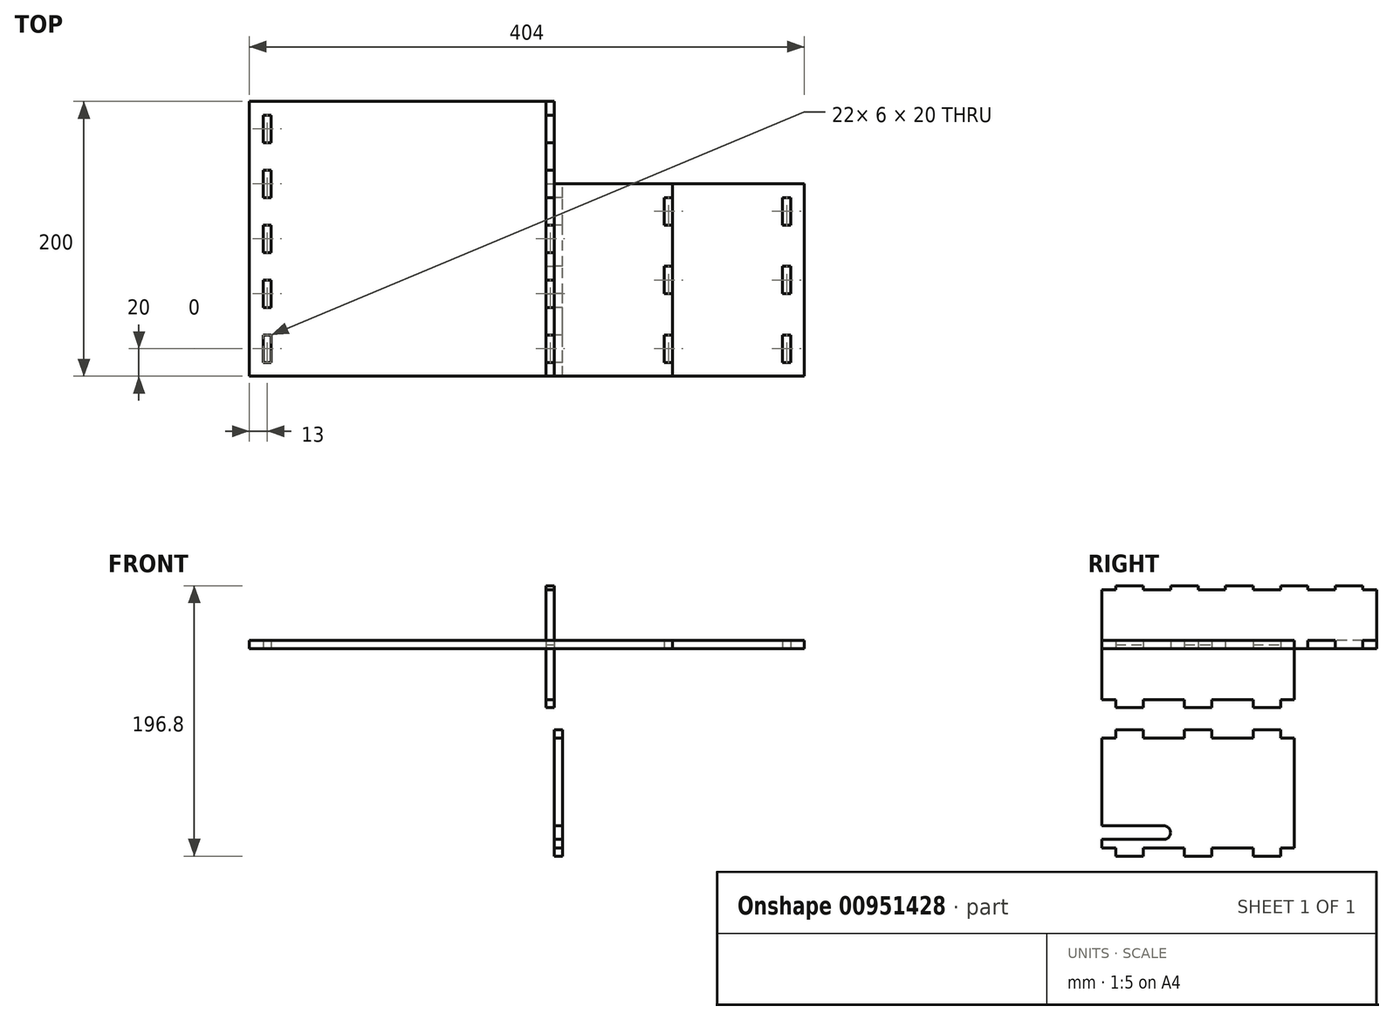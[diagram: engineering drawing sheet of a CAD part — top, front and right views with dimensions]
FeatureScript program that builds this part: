
annotation { "Feature Type Name" : "Feature", "Feature Type Description" : "" }
export const myFeature = defineFeature(function(context is Context, id is Id, definition is map)
    precondition{}
    {
        {
            var Q0;
            Q0=qCreatedBy(makeId("Top.planeOp"),FACE);
            var sketch = newSketch(context, id + "F0", { "sketchPlane" : qUnion([Q0])});
            skLineSegment(sketch, "E0.bottom", {"start": v(0, 200) * mm, "end": v(-222, 200) * mm});
            skLineSegment(sketch, "E0.top", {"start": v(-222, 0) * mm, "end": v(0, 0) * mm});
            skLineSegment(sketch, "E0.left", {"start": v(-222, 200) * mm, "end": v(-222, 0) * mm});
            skLineSegment(sketch, "E0.right", {"start": v(0, 200) * mm, "end": v(0, 0) * mm});
            skLineSegment(sketch, "E1.bottom", {"start": v(0, 0) * mm, "end": v(172, 0) * mm});
            skLineSegment(sketch, "E1.top", {"start": v(0, 140) * mm, "end": v(172, 140) * mm});
            skLineSegment(sketch, "E1.left", {"start": v(0, 0) * mm, "end": v(0, 140) * mm});
            skLineSegment(sketch, "E1.right", {"start": v(172, 0) * mm, "end": v(172, 140) * mm});
            skLineSegment(sketch, "E2.bottom", {"start": v(0, 0) * mm, "end": v(86, 0) * mm});
            skLineSegment(sketch, "E2.top", {"start": v(0, 140) * mm, "end": v(86, 140) * mm});
            skLineSegment(sketch, "E2.right", {"start": v(86, 0) * mm, "end": v(86, 140) * mm});
            skPoint(sketch, "E3.end.orphan", {"position": v(-212, 0) * mm});
            skLineSegment(sketch, "E4.bottom", {"start": v(-212, 190) * mm, "end": v(-206, 190) * mm});
            skLineSegment(sketch, "E4.top", {"start": v(-212, 170) * mm, "end": v(-206, 170) * mm});
            skLineSegment(sketch, "E4.left", {"start": v(-212, 190) * mm, "end": v(-212, 170) * mm});
            skLineSegment(sketch, "E4.right", {"start": v(-206, 190) * mm, "end": v(-206, 170) * mm});
            skLineSegment(sketch, "E5.0.1.0", {"start": v(-212, 150) * mm, "end": v(-212, 130) * mm});
            skLineSegment(sketch, "E5.0.1.1", {"start": v(-206, 150) * mm, "end": v(-206, 130) * mm});
            skLineSegment(sketch, "E5.0.1.2", {"start": v(-212, 150) * mm, "end": v(-206, 150) * mm});
            skLineSegment(sketch, "E5.0.1.3", {"start": v(-212, 130) * mm, "end": v(-206, 130) * mm});
            skLineSegment(sketch, "E5.0.2.0", {"start": v(-212, 110) * mm, "end": v(-212, 90) * mm});
            skLineSegment(sketch, "E5.0.2.1", {"start": v(-206, 110) * mm, "end": v(-206, 90) * mm});
            skLineSegment(sketch, "E5.0.2.2", {"start": v(-212, 110) * mm, "end": v(-206, 110) * mm});
            skLineSegment(sketch, "E5.0.2.3", {"start": v(-212, 90) * mm, "end": v(-206, 90) * mm});
            skLineSegment(sketch, "E5.0.3.0", {"start": v(-212, 70) * mm, "end": v(-212, 50) * mm});
            skLineSegment(sketch, "E5.0.3.1", {"start": v(-206, 70) * mm, "end": v(-206, 50) * mm});
            skLineSegment(sketch, "E5.0.3.2", {"start": v(-212, 70) * mm, "end": v(-206, 70) * mm});
            skLineSegment(sketch, "E5.0.3.3", {"start": v(-212, 50) * mm, "end": v(-206, 50) * mm});
            skLineSegment(sketch, "E5.0.4.0", {"start": v(-212, 30) * mm, "end": v(-212, 10) * mm});
            skLineSegment(sketch, "E5.0.4.1", {"start": v(-206, 30) * mm, "end": v(-206, 10) * mm});
            skLineSegment(sketch, "E5.0.4.2", {"start": v(-212, 30) * mm, "end": v(-206, 30) * mm});
            skLineSegment(sketch, "E5.0.4.3", {"start": v(-212, 10) * mm, "end": v(-206, 10) * mm});
            skLineSegment(sketch, "E5.direction1", {"start": v(-212, 170) * mm, "end": v(-187, 170) * mm, "construction": true});
            skLineSegment(sketch, "E5.direction2", {"start": v(-212, 170) * mm, "end": v(-212, 130) * mm, "construction": true});
            skPoint(sketch, "E6.start.orphan", {"position": v(-6, 200) * mm});
            skLineSegment(sketch, "E7.bottom", {"start": v(0, 190) * mm, "end": v(-6, 190) * mm});
            skLineSegment(sketch, "E7.top", {"start": v(0, 170) * mm, "end": v(-6, 170) * mm});
            skLineSegment(sketch, "E7.left", {"start": v(0, 190) * mm, "end": v(0, 170) * mm});
            skLineSegment(sketch, "E7.right", {"start": v(-6, 190) * mm, "end": v(-6, 170) * mm});
            skLineSegment(sketch, "E8.0.1.0", {"start": v(0, 150) * mm, "end": v(0, 130) * mm});
            skLineSegment(sketch, "E8.0.1.1", {"start": v(0, 130) * mm, "end": v(-6, 130) * mm});
            skLineSegment(sketch, "E8.0.1.2", {"start": v(-6, 150) * mm, "end": v(-6, 130) * mm});
            skLineSegment(sketch, "E8.0.1.3", {"start": v(0, 150) * mm, "end": v(-6, 150) * mm});
            skLineSegment(sketch, "E8.0.2.0", {"start": v(0, 110) * mm, "end": v(0, 90) * mm});
            skLineSegment(sketch, "E8.0.2.1", {"start": v(0, 90) * mm, "end": v(-6, 90) * mm});
            skLineSegment(sketch, "E8.0.2.2", {"start": v(-6, 110) * mm, "end": v(-6, 90) * mm});
            skLineSegment(sketch, "E8.0.2.3", {"start": v(0, 110) * mm, "end": v(-6, 110) * mm});
            skLineSegment(sketch, "E8.0.3.0", {"start": v(0, 70) * mm, "end": v(0, 50) * mm});
            skLineSegment(sketch, "E8.0.3.1", {"start": v(0, 50) * mm, "end": v(-6, 50) * mm});
            skLineSegment(sketch, "E8.0.3.2", {"start": v(-6, 70) * mm, "end": v(-6, 50) * mm});
            skLineSegment(sketch, "E8.0.3.3", {"start": v(0, 70) * mm, "end": v(-6, 70) * mm});
            skLineSegment(sketch, "E8.0.4.0", {"start": v(0, 30) * mm, "end": v(0, 10) * mm});
            skLineSegment(sketch, "E8.0.4.1", {"start": v(0, 10) * mm, "end": v(-6, 10) * mm});
            skLineSegment(sketch, "E8.0.4.2", {"start": v(-6, 30) * mm, "end": v(-6, 10) * mm});
            skLineSegment(sketch, "E8.0.4.3", {"start": v(0, 30) * mm, "end": v(-6, 30) * mm});
            skLineSegment(sketch, "E8.direction1", {"start": v(-6, 170) * mm, "end": v(19, 170) * mm, "construction": true});
            skLineSegment(sketch, "E8.direction2", {"start": v(-6, 170) * mm, "end": v(-6, 130) * mm, "construction": true});
            skLineSegment(sketch, "E9.bottom", {"start": v(172, 10) * mm, "end": v(166, 10) * mm});
            skLineSegment(sketch, "E9.top", {"start": v(172, 30) * mm, "end": v(166, 30) * mm});
            skLineSegment(sketch, "E9.left", {"start": v(172, 10) * mm, "end": v(172, 30) * mm});
            skLineSegment(sketch, "E9.right", {"start": v(166, 10) * mm, "end": v(166, 30) * mm});
            skLineSegment(sketch, "E10.0.1.0", {"start": v(172, 80) * mm, "end": v(166, 80) * mm});
            skLineSegment(sketch, "E10.0.1.1", {"start": v(172, 60) * mm, "end": v(166, 60) * mm});
            skLineSegment(sketch, "E10.0.1.2", {"start": v(166, 60) * mm, "end": v(166, 80) * mm});
            skLineSegment(sketch, "E10.0.1.3", {"start": v(172, 60) * mm, "end": v(172, 80) * mm});
            skLineSegment(sketch, "E10.0.2.0", {"start": v(172, 130) * mm, "end": v(166, 130) * mm});
            skLineSegment(sketch, "E10.0.2.1", {"start": v(172, 110) * mm, "end": v(166, 110) * mm});
            skLineSegment(sketch, "E10.0.2.2", {"start": v(166, 110) * mm, "end": v(166, 130) * mm});
            skLineSegment(sketch, "E10.0.2.3", {"start": v(172, 110) * mm, "end": v(172, 130) * mm});
            skLineSegment(sketch, "E10.1.0.0", {"start": v(86, 30) * mm, "end": v(80, 30) * mm});
            skLineSegment(sketch, "E10.1.0.1", {"start": v(86, 10) * mm, "end": v(80, 10) * mm});
            skLineSegment(sketch, "E10.1.0.2", {"start": v(80, 10) * mm, "end": v(80, 30) * mm});
            skLineSegment(sketch, "E10.1.0.3", {"start": v(86, 10) * mm, "end": v(86, 30) * mm});
            skLineSegment(sketch, "E10.1.1.0", {"start": v(86, 80) * mm, "end": v(80, 80) * mm});
            skLineSegment(sketch, "E10.1.1.1", {"start": v(86, 60) * mm, "end": v(80, 60) * mm});
            skLineSegment(sketch, "E10.1.1.2", {"start": v(80, 60) * mm, "end": v(80, 80) * mm});
            skLineSegment(sketch, "E10.1.1.3", {"start": v(86, 60) * mm, "end": v(86, 80) * mm});
            skLineSegment(sketch, "E10.1.2.0", {"start": v(86, 130) * mm, "end": v(80, 130) * mm});
            skLineSegment(sketch, "E10.1.2.1", {"start": v(86, 110) * mm, "end": v(80, 110) * mm});
            skLineSegment(sketch, "E10.1.2.2", {"start": v(80, 110) * mm, "end": v(80, 130) * mm});
            skLineSegment(sketch, "E10.1.2.3", {"start": v(86, 110) * mm, "end": v(86, 130) * mm});
            skLineSegment(sketch, "E10.direction1", {"start": v(166, 10) * mm, "end": v(80, 10) * mm, "construction": true});
            skLineSegment(sketch, "E10.direction2", {"start": v(166, 10) * mm, "end": v(166, 60) * mm, "construction": true});
            skLineSegment(sketch, "E11.bottom", {"start": v(172, 140) * mm, "end": v(182, 140) * mm});
            skLineSegment(sketch, "E11.top", {"start": v(172, 0) * mm, "end": v(182, 0) * mm});
            skLineSegment(sketch, "E11.left", {"start": v(172, 140) * mm, "end": v(172, 0) * mm});
            skLineSegment(sketch, "E11.right", {"start": v(182, 140) * mm, "end": v(182, 0) * mm});
            skSolve(sketch);
        }
        {
            var Q0;
            Q0=makeQuery(id+"F0.imprint","IMPRINT",FACE,{"disambiguationData":[TD([[makeQuery(id+"F0.imprint","IMPRINT",EDGE,{"derivedFrom":sQuery(id+"F0.wireOp",EDGE,"E0.bottom")}),-1.0]])]});
            var Q1;
            {var subQ10=sQuery(id+"F0.wireOp",EDGE,"E9.bottom");Q1=makeQuery(id+"F0.imprint","IMPRINT",FACE,{"disambiguationData":[TD([[makeQuery(id+"F0.imprint","IMPRINT",EDGE,{"derivedFrom":subQ10}),1.0]])]});}
            var Q2;
            {var subQ14=sQuery(id+"F0.wireOp",EDGE,"E10.1.0.0");Q2=makeQuery(id+"F0.imprint","IMPRINT",FACE,{"disambiguationData":[TD([[makeQuery(id+"F0.imprint","IMPRINT",EDGE,{"derivedFrom":subQ14}),-1.0]])]});}
            var Q3;
            {var subQ5=sQuery(id+"F0.wireOp",EDGE,"E0.bottom");Q3=makeQuery(id+"F0.imprint","IMPRINT",FACE,{"disambiguationData":[TD([[makeQuery(id+"F0.imprint","IMPRINT",EDGE,{"derivedFrom":subQ5}),1.0]])]});}
            var Q4;
            {var subQ5=sQuery(id+"F0.wireOp",EDGE,"E0.bottom");Q4=makeQuery(id+"F0.imprint","IMPRINT",FACE,{"disambiguationData":[TD([[makeQuery(id+"F0.imprint","IMPRINT",EDGE,{"derivedFrom":subQ5}),1.0]])]});}
            var Q5;
            {var subQ7=sQuery(id+"F0.wireOp",EDGE,"E11.bottom");Q5=makeQuery(id+"F0.imprint","IMPRINT",FACE,{"disambiguationData":[TD([[makeQuery(id+"F0.imprint","IMPRINT",EDGE,{"derivedFrom":subQ7}),-1.0]])]});}
            extrude(context, id + "F1", {"entities" : qUnion([Q0, Q1, Q2, Q3, Q4, Q5]), "depth" : 6 * mm, "offsetDistance" : 25 * mm});
        }
        {
            var Q0;
            Q0=makeQuery(id+"F0.imprint","IMPRINT",FACE,{"disambiguationData":[TD([[makeQuery(id+"F0.imprint","IMPRINT",EDGE,{"derivedFrom":sQuery(id+"F0.wireOp",EDGE,"E0.bottom")}),-1.0]])]});
            var Q1;
            {var subQ14=sQuery(id+"F0.wireOp",EDGE,"E10.1.0.0");Q1=makeQuery(id+"F0.imprint","IMPRINT",FACE,{"disambiguationData":[TD([[makeQuery(id+"F0.imprint","IMPRINT",EDGE,{"derivedFrom":subQ14}),-1.0]])]});}
            var Q2;
            {var subQ5=sQuery(id+"F0.wireOp",EDGE,"E0.bottom");Q2=makeQuery(id+"F0.imprint","IMPRINT",FACE,{"disambiguationData":[TD([[makeQuery(id+"F0.imprint","IMPRINT",EDGE,{"derivedFrom":subQ5}),1.0]])]});}
            extrude(context, id + "F2", {"entities" : qUnion([Q0, Q1, Q2]), "depth" : 6 * mm, "offsetDistance" : 25 * mm});
        }
        {
            var Q0;
            Q0=qCreatedBy(makeId("Right.planeOp"),FACE);
            var sketch = newSketch(context, id + "F3", { "sketchPlane" : qUnion([Q0])});
            skLineSegment(sketch, "E12.bottom", {"start": v(0, 6) * mm, "end": v(200, 6) * mm});
            skLineSegment(sketch, "E12.top", {"start": v(0, 43) * mm, "end": v(200, 43) * mm});
            skLineSegment(sketch, "E12.left", {"start": v(0, 6) * mm, "end": v(0, 43) * mm});
            skLineSegment(sketch, "E12.right", {"start": v(200, 6) * mm, "end": v(200, 43) * mm});
            skLineSegment(sketch, "E13.bottom", {"start": v(10, 6) * mm, "end": v(30, 6) * mm});
            skLineSegment(sketch, "E13.top", {"start": v(10, 0) * mm, "end": v(30, 0) * mm});
            skLineSegment(sketch, "E13.left", {"start": v(10, 6) * mm, "end": v(10, 0) * mm});
            skLineSegment(sketch, "E13.right", {"start": v(30, 6) * mm, "end": v(30, 0) * mm});
            skLineSegment(sketch, "E14.1.0.0", {"start": v(50, 6) * mm, "end": v(50, 0) * mm});
            skLineSegment(sketch, "E14.1.0.1", {"start": v(70, 6) * mm, "end": v(70, 0) * mm});
            skLineSegment(sketch, "E14.1.0.2", {"start": v(50, 0) * mm, "end": v(70, 0) * mm});
            skLineSegment(sketch, "E14.1.0.3", {"start": v(50, 6) * mm, "end": v(70, 6) * mm});
            skLineSegment(sketch, "E14.2.0.0", {"start": v(90, 6) * mm, "end": v(90, 0) * mm});
            skLineSegment(sketch, "E14.2.0.1", {"start": v(110, 6) * mm, "end": v(110, 0) * mm});
            skLineSegment(sketch, "E14.2.0.2", {"start": v(90, 0) * mm, "end": v(110, 0) * mm});
            skLineSegment(sketch, "E14.2.0.3", {"start": v(90, 6) * mm, "end": v(110, 6) * mm});
            skLineSegment(sketch, "E14.3.0.0", {"start": v(130, 6) * mm, "end": v(130, 0) * mm});
            skLineSegment(sketch, "E14.3.0.1", {"start": v(150, 6) * mm, "end": v(150, 0) * mm});
            skLineSegment(sketch, "E14.3.0.2", {"start": v(130, 0) * mm, "end": v(150, 0) * mm});
            skLineSegment(sketch, "E14.3.0.3", {"start": v(130, 6) * mm, "end": v(150, 6) * mm});
            skLineSegment(sketch, "E14.4.0.0", {"start": v(170, 6) * mm, "end": v(170, 0) * mm});
            skLineSegment(sketch, "E14.4.0.1", {"start": v(190, 6) * mm, "end": v(190, 0) * mm});
            skLineSegment(sketch, "E14.4.0.2", {"start": v(170, 0) * mm, "end": v(190, 0) * mm});
            skLineSegment(sketch, "E14.4.0.3", {"start": v(170, 6) * mm, "end": v(190, 6) * mm});
            skLineSegment(sketch, "E14.direction1", {"start": v(10, 0) * mm, "end": v(50, 0) * mm, "construction": true});
            skLineSegment(sketch, "E15.bottom", {"start": v(10, 43) * mm, "end": v(30, 43) * mm});
            skLineSegment(sketch, "E15.top", {"start": v(10, 45.8) * mm, "end": v(30, 45.8) * mm});
            skLineSegment(sketch, "E15.left", {"start": v(10, 43) * mm, "end": v(10, 45.8) * mm});
            skLineSegment(sketch, "E15.right", {"start": v(30, 43) * mm, "end": v(30, 45.8) * mm});
            skLineSegment(sketch, "E16.1.0.0", {"start": v(50, 43) * mm, "end": v(70, 43) * mm});
            skLineSegment(sketch, "E16.1.0.1", {"start": v(50, 43) * mm, "end": v(50, 45.8) * mm});
            skLineSegment(sketch, "E16.1.0.2", {"start": v(70, 43) * mm, "end": v(70, 45.8) * mm});
            skLineSegment(sketch, "E16.1.0.3", {"start": v(50, 45.8) * mm, "end": v(70, 45.8) * mm});
            skLineSegment(sketch, "E16.2.0.0", {"start": v(90, 43) * mm, "end": v(110, 43) * mm});
            skLineSegment(sketch, "E16.2.0.1", {"start": v(90, 43) * mm, "end": v(90, 45.8) * mm});
            skLineSegment(sketch, "E16.2.0.2", {"start": v(110, 43) * mm, "end": v(110, 45.8) * mm});
            skLineSegment(sketch, "E16.2.0.3", {"start": v(90, 45.8) * mm, "end": v(110, 45.8) * mm});
            skLineSegment(sketch, "E16.3.0.0", {"start": v(130, 43) * mm, "end": v(150, 43) * mm});
            skLineSegment(sketch, "E16.3.0.1", {"start": v(130, 43) * mm, "end": v(130, 45.8) * mm});
            skLineSegment(sketch, "E16.3.0.2", {"start": v(150, 43) * mm, "end": v(150, 45.8) * mm});
            skLineSegment(sketch, "E16.3.0.3", {"start": v(130, 45.8) * mm, "end": v(150, 45.8) * mm});
            skLineSegment(sketch, "E16.4.0.0", {"start": v(170, 43) * mm, "end": v(190, 43) * mm});
            skLineSegment(sketch, "E16.4.0.1", {"start": v(170, 43) * mm, "end": v(170, 45.8) * mm});
            skLineSegment(sketch, "E16.4.0.2", {"start": v(190, 43) * mm, "end": v(190, 45.8) * mm});
            skLineSegment(sketch, "E16.4.0.3", {"start": v(170, 45.8) * mm, "end": v(190, 45.8) * mm});
            skLineSegment(sketch, "E16.direction1", {"start": v(10, 43) * mm, "end": v(50, 43) * mm, "construction": true});
            skSolve(sketch);
        }
        {
            var Q0;
            {var subQ0=sQuery(id+"F3.wireOp",EDGE,"E14.1.0.0");var subQ6=sQuery(id+"F3.wireOp",EDGE,"E16.4.0.1");var subQ22=sQuery(id+"F3.wireOp",EDGE,"E16.2.0.1");var subQ27=sQuery(id+"F3.wireOp",EDGE,"E14.3.0.0");var subQ32=sQuery(id+"F3.wireOp",EDGE,"E16.1.0.1");var subQ37=sQuery(id+"F3.wireOp",EDGE,"E14.4.0.0");var subQ42=sQuery(id+"F3.wireOp",EDGE,"E14.2.0.0");var subQ47=sQuery(id+"F3.wireOp",EDGE,"E12.left");var subQ49=sQuery(id+"F3.wireOp",EDGE,"E16.3.0.1");Q0=qUnion([makeQuery(id+"F3.imprint","IMPRINT",FACE,{"disambiguationData":[TD([[makeQuery(id+"F3.imprint","IMPRINT",EDGE,{"derivedFrom":subQ49}),-1.0]])]}),makeQuery(id+"F3.imprint","IMPRINT",FACE,{"disambiguationData":[TD([[makeQuery(id+"F3.imprint","IMPRINT",EDGE,{"derivedFrom":subQ47}),-1.0]])]}),makeQuery(id+"F3.imprint","IMPRINT",FACE,{"disambiguationData":[TD([[makeQuery(id+"F3.imprint","IMPRINT",EDGE,{"derivedFrom":subQ42}),1.0]])]}),makeQuery(id+"F3.imprint","IMPRINT",FACE,{"disambiguationData":[TD([[makeQuery(id+"F3.imprint","IMPRINT",EDGE,{"derivedFrom":subQ37}),1.0]])]}),makeQuery(id+"F3.imprint","IMPRINT",FACE,{"disambiguationData":[TD([[makeQuery(id+"F3.imprint","IMPRINT",EDGE,{"derivedFrom":subQ32}),-1.0]])]}),makeQuery(id+"F3.imprint","IMPRINT",FACE,{"disambiguationData":[TD([[makeQuery(id+"F3.imprint","IMPRINT",EDGE,{"derivedFrom":subQ27}),1.0]])]}),makeQuery(id+"F3.imprint","IMPRINT",FACE,{"disambiguationData":[TD([[makeQuery(id+"F3.imprint","IMPRINT",EDGE,{"derivedFrom":subQ22}),-1.0]])]}),makeQuery(id+"F3.imprint","IMPRINT",FACE,{"disambiguationData":[TD([[makeQuery(id+"F3.imprint","IMPRINT",EDGE,{"derivedFrom":sQuery(id+"F3.wireOp",EDGE,"E15.top")}),-1.0]])]}),makeQuery(id+"F3.imprint","IMPRINT",FACE,{"disambiguationData":[TD([[makeQuery(id+"F3.imprint","IMPRINT",EDGE,{"derivedFrom":sQuery(id+"F3.wireOp",EDGE,"E13.top")}),1.0]])]}),makeQuery(id+"F3.imprint","IMPRINT",FACE,{"disambiguationData":[TD([[makeQuery(id+"F3.imprint","IMPRINT",EDGE,{"derivedFrom":subQ6}),-1.0]])]}),makeQuery(id+"F3.imprint","IMPRINT",FACE,{"disambiguationData":[TD([[makeQuery(id+"F3.imprint","IMPRINT",EDGE,{"derivedFrom":subQ0}),1.0]])]})]);}
            extrude(context, id + "F4", {"entities" : qUnion([Q0]), "oppositeDirection" : true, "depth" : 6 * mm, "offsetDistance" : 25 * mm});
        }
        {
            var Q0;
            Q0=qCreatedBy(makeId("Right.planeOp"),FACE);
            var sketch = newSketch(context, id + "F5", { "sketchPlane" : qUnion([Q0])});
            skLineSegment(sketch, "E17.bottom", {"start": v(0, 0) * mm, "end": v(140, 0) * mm});
            skLineSegment(sketch, "E17.top", {"start": v(0, -37) * mm, "end": v(140, -37) * mm});
            skLineSegment(sketch, "E17.left", {"start": v(0, 0) * mm, "end": v(0, -37) * mm});
            skLineSegment(sketch, "E17.right", {"start": v(140, 0) * mm, "end": v(140, -37) * mm});
            skLineSegment(sketch, "E18.bottom", {"start": v(10, -37) * mm, "end": v(30, -37) * mm});
            skLineSegment(sketch, "E18.top", {"start": v(10, -43) * mm, "end": v(30, -43) * mm});
            skLineSegment(sketch, "E18.left", {"start": v(10, -37) * mm, "end": v(10, -43) * mm});
            skLineSegment(sketch, "E18.right", {"start": v(30, -37) * mm, "end": v(30, -43) * mm});
            skLineSegment(sketch, "E19.0.1.0", {"start": v(30, 3) * mm, "end": v(30, -3) * mm});
            skLineSegment(sketch, "E19.0.1.1", {"start": v(10, -3) * mm, "end": v(30, -3) * mm});
            skLineSegment(sketch, "E19.0.1.2", {"start": v(10, 3) * mm, "end": v(10, -3) * mm});
            skLineSegment(sketch, "E19.0.1.3", {"start": v(10, 3) * mm, "end": v(30, 3) * mm});
            skLineSegment(sketch, "E19.1.0.0", {"start": v(80, -37) * mm, "end": v(80, -43) * mm});
            skLineSegment(sketch, "E19.1.0.1", {"start": v(60, -43) * mm, "end": v(80, -43) * mm});
            skLineSegment(sketch, "E19.1.0.2", {"start": v(60, -37) * mm, "end": v(60, -43) * mm});
            skLineSegment(sketch, "E19.1.0.3", {"start": v(60, -37) * mm, "end": v(80, -37) * mm});
            skLineSegment(sketch, "E19.1.1.0", {"start": v(80, 3) * mm, "end": v(80, -3) * mm});
            skLineSegment(sketch, "E19.1.1.1", {"start": v(60, -3) * mm, "end": v(80, -3) * mm});
            skLineSegment(sketch, "E19.1.1.2", {"start": v(60, 3) * mm, "end": v(60, -3) * mm});
            skLineSegment(sketch, "E19.1.1.3", {"start": v(60, 3) * mm, "end": v(80, 3) * mm});
            skLineSegment(sketch, "E19.2.0.0", {"start": v(130, -37) * mm, "end": v(130, -43) * mm});
            skLineSegment(sketch, "E19.2.0.1", {"start": v(110, -43) * mm, "end": v(130, -43) * mm});
            skLineSegment(sketch, "E19.2.0.2", {"start": v(110, -37) * mm, "end": v(110, -43) * mm});
            skLineSegment(sketch, "E19.2.0.3", {"start": v(110, -37) * mm, "end": v(130, -37) * mm});
            skLineSegment(sketch, "E19.2.1.0", {"start": v(130, 3) * mm, "end": v(130, -3) * mm});
            skLineSegment(sketch, "E19.2.1.1", {"start": v(110, -3) * mm, "end": v(130, -3) * mm});
            skLineSegment(sketch, "E19.2.1.2", {"start": v(110, 3) * mm, "end": v(110, -3) * mm});
            skLineSegment(sketch, "E19.2.1.3", {"start": v(110, 3) * mm, "end": v(130, 3) * mm});
            skLineSegment(sketch, "E19.direction1", {"start": v(10, -43) * mm, "end": v(60, -43) * mm, "construction": true});
            skLineSegment(sketch, "E19.direction2", {"start": v(10, -43) * mm, "end": v(10, -3) * mm, "construction": true});
            skSolve(sketch);
        }
        {
            var Q0;
            {var subQ22=sQuery(id+"F5.wireOp",EDGE,"E17.left");Q0=makeQuery(id+"F5.imprint","IMPRINT",FACE,{"disambiguationData":[TD([[makeQuery(id+"F5.imprint","IMPRINT",EDGE,{"derivedFrom":subQ22}),1.0]])]});}
            var Q1;
            {var subQ5=sQuery(id+"F5.wireOp",EDGE,"E19.0.1.1");Q1=makeQuery(id+"F5.imprint","IMPRINT",FACE,{"disambiguationData":[TD([[makeQuery(id+"F5.imprint","IMPRINT",EDGE,{"derivedFrom":subQ5}),1.0]])]});}
            var Q2;
            {var subQ5=sQuery(id+"F5.wireOp",EDGE,"E19.0.1.3");Q2=makeQuery(id+"F5.imprint","IMPRINT",FACE,{"disambiguationData":[TD([[makeQuery(id+"F5.imprint","IMPRINT",EDGE,{"derivedFrom":subQ5}),-1.0]])]});}
            var Q3;
            {var subQ5=sQuery(id+"F5.wireOp",EDGE,"E19.1.1.3");Q3=makeQuery(id+"F5.imprint","IMPRINT",FACE,{"disambiguationData":[TD([[makeQuery(id+"F5.imprint","IMPRINT",EDGE,{"derivedFrom":subQ5}),-1.0]])]});}
            var Q4;
            {var subQ5=sQuery(id+"F5.wireOp",EDGE,"E19.1.1.1");Q4=makeQuery(id+"F5.imprint","IMPRINT",FACE,{"disambiguationData":[TD([[makeQuery(id+"F5.imprint","IMPRINT",EDGE,{"derivedFrom":subQ5}),1.0]])]});}
            var Q5;
            {var subQ5=sQuery(id+"F5.wireOp",EDGE,"E19.2.1.3");Q5=makeQuery(id+"F5.imprint","IMPRINT",FACE,{"disambiguationData":[TD([[makeQuery(id+"F5.imprint","IMPRINT",EDGE,{"derivedFrom":subQ5}),-1.0]])]});}
            var Q6;
            {var subQ5=sQuery(id+"F5.wireOp",EDGE,"E19.2.1.1");Q6=makeQuery(id+"F5.imprint","IMPRINT",FACE,{"disambiguationData":[TD([[makeQuery(id+"F5.imprint","IMPRINT",EDGE,{"derivedFrom":subQ5}),1.0]])]});}
            var Q7;
            {var subQ0=sQuery(id+"F5.wireOp",EDGE,"E19.2.0.0");Q7=makeQuery(id+"F5.imprint","IMPRINT",FACE,{"disambiguationData":[TD([[makeQuery(id+"F5.imprint","IMPRINT",EDGE,{"derivedFrom":subQ0}),-1.0]])]});}
            var Q8;
            {var subQ0=sQuery(id+"F5.wireOp",EDGE,"E19.1.0.0");Q8=makeQuery(id+"F5.imprint","IMPRINT",FACE,{"disambiguationData":[TD([[makeQuery(id+"F5.imprint","IMPRINT",EDGE,{"derivedFrom":subQ0}),-1.0]])]});}
            var Q9;
            Q9=makeQuery(id+"F5.imprint","IMPRINT",FACE,{"disambiguationData":[TD([[makeQuery(id+"F5.imprint","IMPRINT",EDGE,{"derivedFrom":sQuery(id+"F5.wireOp",EDGE,"E18.top")}),1.0]])]});
            extrude(context, id + "F6", {"entities" : qUnion([Q0, Q1, Q2, Q3, Q4, Q5, Q6, Q7, Q8, Q9]), "oppositeDirection" : true, "depth" : 6 * mm, "offsetDistance" : 25 * mm});
        }
        {
            var Q0;
            Q0=qCreatedBy(makeId("Right.planeOp"),FACE);
            var sketch = newSketch(context, id + "F7", { "sketchPlane" : qUnion([Q0])});
            skLineSegment(sketch, "E20.bottom", {"start": v(0, -65) * mm, "end": v(140, -65) * mm});
            skLineSegment(sketch, "E20.top", {"start": v(0, -145) * mm, "end": v(140, -145) * mm});
            skLineSegment(sketch, "E20.left", {"start": v(0, -65) * mm, "end": v(0, -128.9) * mm});
            skLineSegment(sketch, "E20.right", {"start": v(140, -65) * mm, "end": v(140, -145) * mm});
            skLineSegment(sketch, "E21.bottom", {"start": v(10, -145) * mm, "end": v(30, -145) * mm});
            skLineSegment(sketch, "E21.top", {"start": v(10, -151) * mm, "end": v(30, -151) * mm});
            skLineSegment(sketch, "E21.left", {"start": v(10, -145) * mm, "end": v(10, -151) * mm});
            skLineSegment(sketch, "E21.right", {"start": v(30, -145) * mm, "end": v(30, -151) * mm});
            skLineSegment(sketch, "E22.0.1.0", {"start": v(30, -59) * mm, "end": v(30, -65) * mm});
            skLineSegment(sketch, "E22.0.1.1", {"start": v(10, -59) * mm, "end": v(30, -59) * mm});
            skLineSegment(sketch, "E22.0.1.2", {"start": v(10, -65) * mm, "end": v(30, -65) * mm});
            skLineSegment(sketch, "E22.0.1.3", {"start": v(10, -59) * mm, "end": v(10, -65) * mm});
            skLineSegment(sketch, "E22.1.0.0", {"start": v(80, -145) * mm, "end": v(80, -151) * mm});
            skLineSegment(sketch, "E22.1.0.1", {"start": v(60, -145) * mm, "end": v(80, -145) * mm});
            skLineSegment(sketch, "E22.1.0.2", {"start": v(60, -151) * mm, "end": v(80, -151) * mm});
            skLineSegment(sketch, "E22.1.0.3", {"start": v(60, -145) * mm, "end": v(60, -151) * mm});
            skLineSegment(sketch, "E22.1.1.0", {"start": v(80, -59) * mm, "end": v(80, -65) * mm});
            skLineSegment(sketch, "E22.1.1.1", {"start": v(60, -59) * mm, "end": v(80, -59) * mm});
            skLineSegment(sketch, "E22.1.1.2", {"start": v(60, -65) * mm, "end": v(80, -65) * mm});
            skLineSegment(sketch, "E22.1.1.3", {"start": v(60, -59) * mm, "end": v(60, -65) * mm});
            skLineSegment(sketch, "E22.2.0.0", {"start": v(130, -145) * mm, "end": v(130, -151) * mm});
            skLineSegment(sketch, "E22.2.0.1", {"start": v(110, -145) * mm, "end": v(130, -145) * mm});
            skLineSegment(sketch, "E22.2.0.2", {"start": v(110, -151) * mm, "end": v(130, -151) * mm});
            skLineSegment(sketch, "E22.2.0.3", {"start": v(110, -145) * mm, "end": v(110, -151) * mm});
            skLineSegment(sketch, "E22.2.1.0", {"start": v(130, -59) * mm, "end": v(130, -65) * mm});
            skLineSegment(sketch, "E22.2.1.1", {"start": v(110, -59) * mm, "end": v(130, -59) * mm});
            skLineSegment(sketch, "E22.2.1.2", {"start": v(110, -65) * mm, "end": v(130, -65) * mm});
            skLineSegment(sketch, "E22.2.1.3", {"start": v(110, -59) * mm, "end": v(110, -65) * mm});
            skLineSegment(sketch, "E22.direction1", {"start": v(10, -151) * mm, "end": v(60, -151) * mm, "construction": true});
            skLineSegment(sketch, "E22.direction2", {"start": v(10, -151) * mm, "end": v(10, -65) * mm, "construction": true});
            skLineSegment(sketch, "E23.bottom", {"start": v(0, -138.9) * mm, "end": v(45, -138.9) * mm});
            skLineSegment(sketch, "E23.top", {"start": v(0, -128.9) * mm, "end": v(45, -128.9) * mm});
            skLineSegment(sketch, "E23.right", {"start": v(50, -133.9) * mm, "end": v(50, -133.9) * mm});
            skPoint(sketch, "E24.visualSharp", {"position": v(50, -128.9) * mm});
            skArc(sketch, "E24.filletArc", {"start": v(50, -133.9) * mm, "mid": v(48.54, -130.36) * mm, "end": v(45, -128.9) * mm});
            skPoint(sketch, "E25.visualSharp", {"position": v(50, -138.9) * mm});
            skArc(sketch, "E25.filletArc", {"start": v(45, -138.9) * mm, "mid": v(48.54, -137.43) * mm, "end": v(50, -133.9) * mm});
            skLineSegment(sketch, "E26.trimOffspring", {"start": v(0, -138.9) * mm, "end": v(0, -145) * mm});
            skSolve(sketch);
        }
        {
            var Q0;
            {var subQ0=sQuery(id+"F7.wireOp",EDGE,"E22.1.1.0");var subQ12=sQuery(id+"F7.wireOp",EDGE,"E22.1.0.0");var subQ21=sQuery(id+"F7.wireOp",EDGE,"E20.left");var subQ23=sQuery(id+"F7.wireOp",EDGE,"E22.2.1.0");var subQ25=sQuery(id+"F7.wireOp",EDGE,"E22.0.1.0");var subQ31=sQuery(id+"F7.wireOp",EDGE,"E22.2.0.0");Q0=qUnion([makeQuery(id+"F7.imprint","IMPRINT",FACE,{"disambiguationData":[TD([[makeQuery(id+"F7.imprint","IMPRINT",EDGE,{"derivedFrom":subQ31}),-1.0]])]}),makeQuery(id+"F7.imprint","IMPRINT",FACE,{"disambiguationData":[TD([[makeQuery(id+"F7.imprint","IMPRINT",EDGE,{"derivedFrom":subQ23}),-1.0]])]}),makeQuery(id+"F7.imprint","IMPRINT",FACE,{"disambiguationData":[TD([[makeQuery(id+"F7.imprint","IMPRINT",EDGE,{"derivedFrom":subQ25}),-1.0]])]}),makeQuery(id+"F7.imprint","IMPRINT",FACE,{"disambiguationData":[TD([[makeQuery(id+"F7.imprint","IMPRINT",EDGE,{"derivedFrom":subQ12}),-1.0]])]}),makeQuery(id+"F7.imprint","IMPRINT",FACE,{"disambiguationData":[TD([[makeQuery(id+"F7.imprint","IMPRINT",EDGE,{"derivedFrom":subQ21}),1.0]])]}),makeQuery(id+"F7.imprint","IMPRINT",FACE,{"disambiguationData":[TD([[makeQuery(id+"F7.imprint","IMPRINT",EDGE,{"derivedFrom":sQuery(id+"F7.wireOp",EDGE,"E21.top")}),1.0]])]}),makeQuery(id+"F7.imprint","IMPRINT",FACE,{"disambiguationData":[TD([[makeQuery(id+"F7.imprint","IMPRINT",EDGE,{"derivedFrom":subQ0}),-1.0]])]})]);}
            extrude(context, id + "F8", {"entities" : qUnion([Q0]), "depth" : 6 * mm, "offsetDistance" : 25 * mm});
        }
    });
